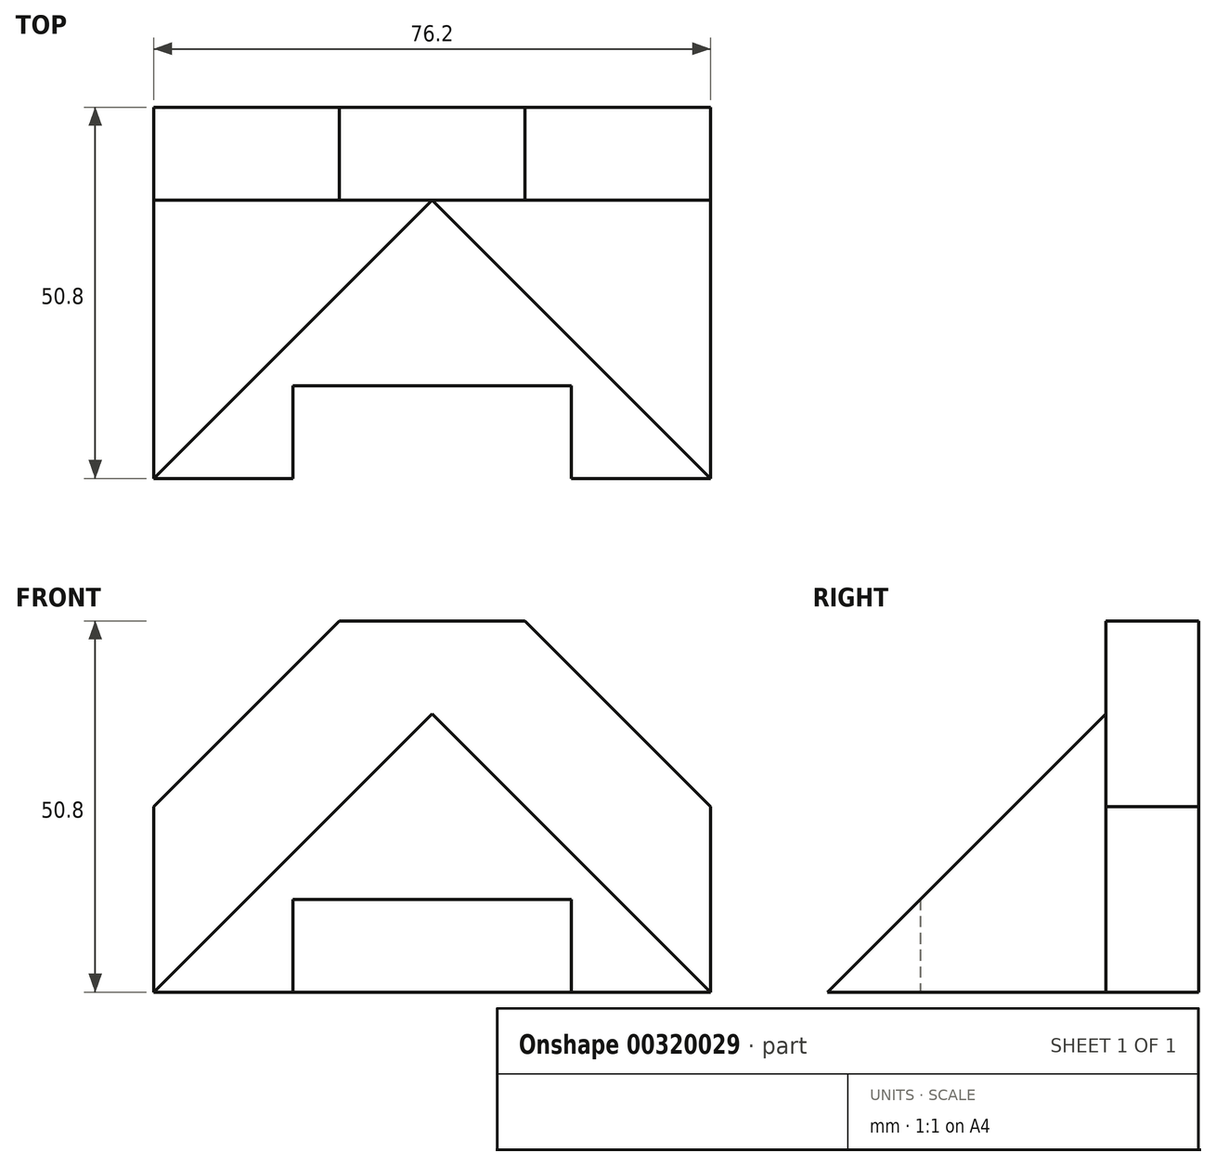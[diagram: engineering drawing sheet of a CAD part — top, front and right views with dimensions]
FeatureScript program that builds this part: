
annotation { "Feature Type Name" : "Feature", "Feature Type Description" : "" }
export const myFeature = defineFeature(function(context is Context, id is Id, definition is map)
    precondition{}
    {
        {
            var Q0;
            Q0=qCreatedBy(makeId("Front.planeOp"),FACE);
            var sketch = newSketch(context, id + "F0", { "sketchPlane" : qUnion([Q0])});
            skLineSegment(sketch, "E0", {"start": v(0, -32.99) * mm, "end": v(0, 43.6) * mm, "construction": true});
            skLineSegment(sketch, "E1", {"start": v(-38.1, 0) * mm, "end": v(38.1, 0) * mm});
            skLineSegment(sketch, "E2", {"start": v(-38.1, 0) * mm, "end": v(0, 38.1) * mm});
            skLineSegment(sketch, "E3", {"start": v(0, 38.1) * mm, "end": v(38.1, 0) * mm});
            skSolve(sketch);
        }
        {
            var Q0;
            Q0 = qSketchRegion(id + "F0", true);
            extrude(context, id + "F1", {"entities" : qUnion([Q0]), "depth" : 38.1 * mm});
        }
        {
            var Q0;
            Q0=qCreatedBy(makeId("Front.planeOp"),FACE);
            var sketch = newSketch(context, id + "F2", { "sketchPlane" : qUnion([Q0])});
            skLineSegment(sketch, "E4.bottom", {"start": v(-38.1, 0) * mm, "end": v(38.1, 0) * mm});
            skLineSegment(sketch, "E4.top", {"start": v(-12.7, 50.8) * mm, "end": v(12.7, 50.8) * mm});
            skLineSegment(sketch, "E4.left", {"start": v(-38.1, 0) * mm, "end": v(-38.1, 25.4) * mm});
            skLineSegment(sketch, "E4.right", {"start": v(38.1, 0) * mm, "end": v(38.1, 25.4) * mm});
            skLineSegment(sketch, "E5", {"start": v(-38.1, 25.4) * mm, "end": v(-12.7, 50.8) * mm});
            skLineSegment(sketch, "E6", {"start": v(12.7, 50.8) * mm, "end": v(38.1, 25.4) * mm});
            skSolve(sketch);
        }
        {
            var Q0;
            Q0 = qSketchRegion(id + "F2", true);
            extrude(context, id + "F3", {"entities" : qUnion([Q0]), "oppositeDirection" : true, "depth" : 12.7 * mm});
        }
        {
            var Q0;
            Q0=makeQuery(id+"F1.opExtrude","SWEPT_FACE",FACE,{"disambiguationData":[OSD([sQuery(id+"F0.wireOp",EDGE,"E1")])]});
            var sketch = newSketch(context, id + "F4", { "sketchPlane" : qUnion([Q0])});
            skLineSegment(sketch, "E7.bottom", {"start": v(-19.05, 38.1) * mm, "end": v(19.05, 38.1) * mm});
            skLineSegment(sketch, "E7.top", {"start": v(-19.05, 25.4) * mm, "end": v(19.05, 25.4) * mm});
            skLineSegment(sketch, "E7.left", {"start": v(-19.05, 38.1) * mm, "end": v(-19.05, 25.4) * mm});
            skLineSegment(sketch, "E7.right", {"start": v(19.05, 38.1) * mm, "end": v(19.05, 25.4) * mm});
            skSolve(sketch);
        }
        {
            var Q0;
            Q0 = qSketchRegion(id + "F4", true);
            extrude(context, id + "F5", {"entities" : qUnion([Q0]), "operationType" : NewBodyOperationType.REMOVE, "endBound" : BoundingType.THROUGH_ALL, "oppositeDirection" : true, "depth" : 25.4 * mm});
        }
        {
            var Q0;
            Q0=qCreatedBy(makeId("Right.planeOp"),FACE);
            var sketch = newSketch(context, id + "F6", { "sketchPlane" : qUnion([Q0])});
            skLineSegment(sketch, "E8.0.0", {"start": v(-25.4, 38.1) * mm, "end": v(-25.4, 19.05) * mm});
            skLineSegment(sketch, "E8.0.1", {"start": v(-25.4, 19.05) * mm, "end": v(-38.1, 19.05) * mm});
            skLineSegment(sketch, "E8.0.2", {"start": v(-38.1, 19.05) * mm, "end": v(-38.1, 0) * mm});
            skLineSegment(sketch, "E8.0.3", {"start": v(-38.1, 0) * mm, "end": v(0, 0) * mm});
            skLineSegment(sketch, "E8.0.4", {"start": v(0, 0) * mm, "end": v(0, 38.1) * mm});
            skLineSegment(sketch, "E8.0.5", {"start": v(0, 38.1) * mm, "end": v(-25.4, 38.1) * mm});
            skLineSegment(sketch, "E9", {"start": v(-38.1, 0) * mm, "end": v(0, 38.1) * mm});
            skSolve(sketch);
        }
        {
            var Q0;
            Q0=makeQuery(id+"F6.imprint","IMPRINT",FACE,{"disambiguationData":[TD([[makeQuery(id+"F6.imprint","IMPRINT",EDGE,{"derivedFrom":sQuery(id+"F6.wireOp",EDGE,"E8.0.0")}),1.0]])]});
            extrude(context, id + "F7", {"entities" : qUnion([Q0]), "operationType" : NewBodyOperationType.REMOVE, "endBound" : BoundingType.THROUGH_ALL, "oppositeDirection" : true, "depth" : 25.4 * mm, "hasSecondDirection" : true, "secondDirectionBound" : SecondDirectionBoundingType.THROUGH_ALL, "secondDirectionOppositeDirection" : false, "secondDirectionDepth" : 25.4 * mm});
        }
    });
